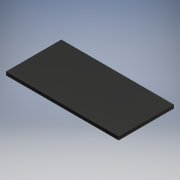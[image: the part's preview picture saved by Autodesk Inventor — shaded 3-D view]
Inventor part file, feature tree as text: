
AUTODESK INVENTOR PART (.ipt)
format: ipt  version: 2018 (Build 220112000, 112)  size: 91,648 bytes
history: native  units: mm
features: extrude x1, sketch x1
ambient origin geometry x8: Origin, YZ Plane, XZ Plane, XY Plane, X Axis, Y Axis, Z Axis, Center Point
bodies: Solid1 (feature_tree)
feature tree (2):
  extrude  "Extrusion1"  Depth=49.027mm
  sketch  "Sketch1"  dims[d0=100.0mm d1=49.027mm d2=3.0mm d3=0.0mm]
